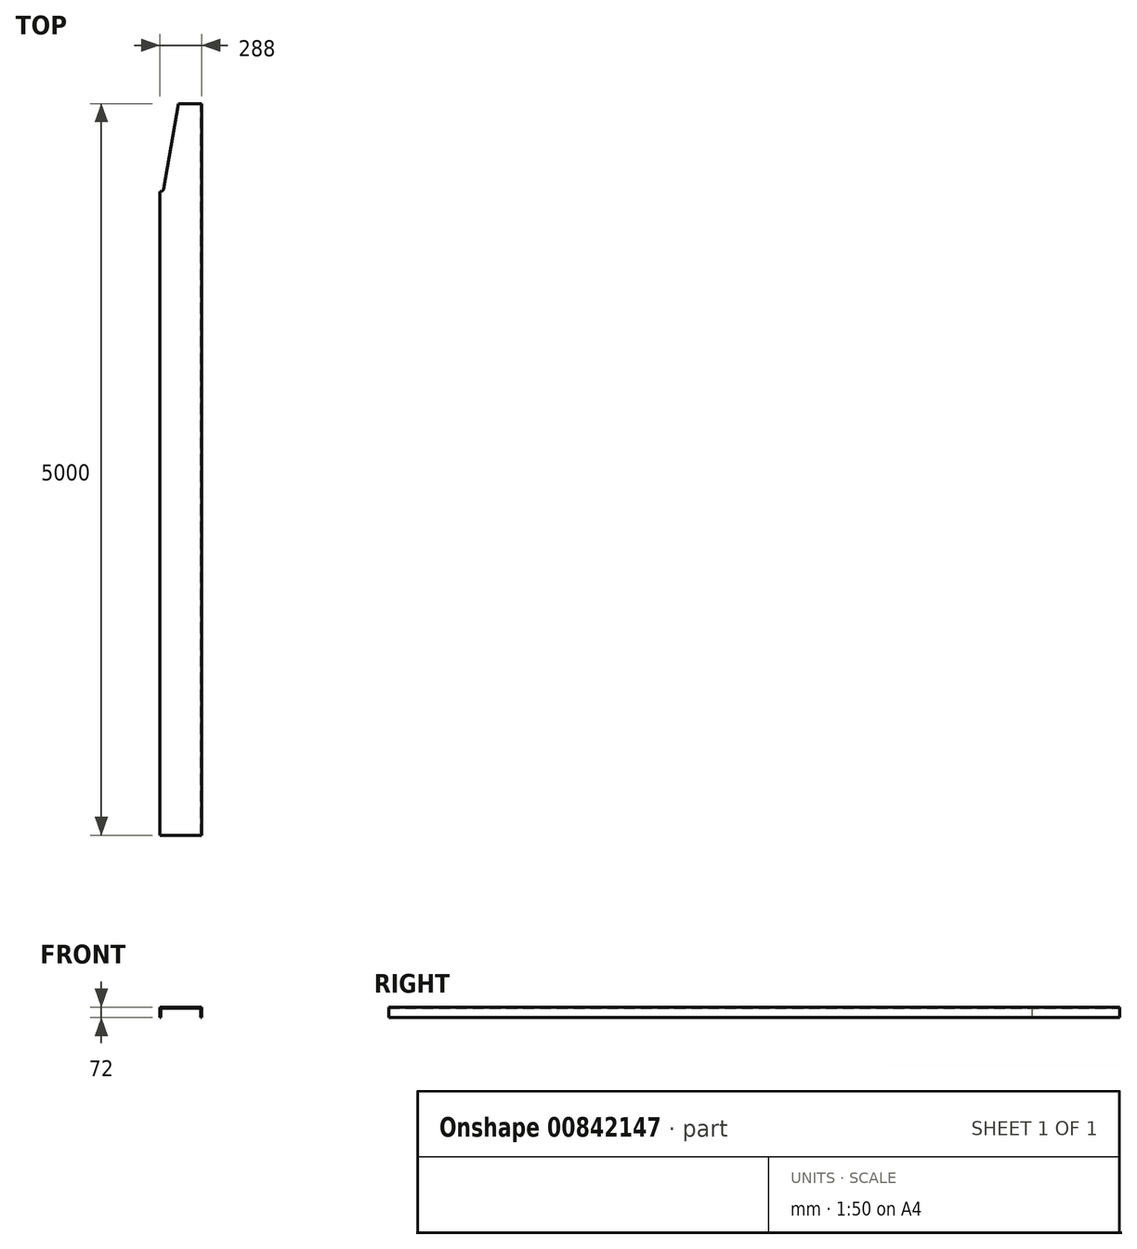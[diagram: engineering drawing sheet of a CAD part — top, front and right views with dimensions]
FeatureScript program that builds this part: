
annotation { "Feature Type Name" : "Feature", "Feature Type Description" : "" }
export const myFeature = defineFeature(function(context is Context, id is Id, definition is map)
    precondition{}
    {
        {
            var Q0;
            Q0=qCreatedBy(makeId("Front.planeOp"),FACE);
            var sketch = newSketch(context, id + "F0", { "sketchPlane" : qUnion([Q0])});
            skLineSegment(sketch, "E0", {"start": v(0, 8) * mm, "end": v(-144, 8) * mm});
            skLineSegment(sketch, "E1", {"start": v(-144, 8) * mm, "end": v(-144, -64) * mm});
            skLineSegment(sketch, "E2", {"start": v(-144, -64) * mm, "end": v(-136, -64) * mm});
            skLineSegment(sketch, "E3", {"start": v(-136, -64) * mm, "end": v(-136, -8) * mm});
            skLineSegment(sketch, "E4", {"start": v(-128, 0) * mm, "end": v(0, 0) * mm});
            skLineSegment(sketch, "E5", {"start": v(0, 50.67) * mm, "end": v(0, -39.29) * mm, "construction": true});
            skPoint(sketch, "E6.visualSharp", {"position": v(-136, 0) * mm});
            skArc(sketch, "E6.filletArc", {"start": v(-128, 0) * mm, "mid": v(-133.66, -2.34) * mm, "end": v(-136, -8) * mm});
            skLineSegment(sketch, "E7.MirrorCS", {"start": v(144, -64) * mm, "end": v(136, -64) * mm});
            skArc(sketch, "E8.MirrorCS", {"start": v(128, 0) * mm, "mid": v(133.66, -2.34) * mm, "end": v(136, -8) * mm});
            skLineSegment(sketch, "E9.MirrorCS", {"start": v(128, 0) * mm, "end": v(0, 0) * mm});
            skLineSegment(sketch, "E10.MirrorCS", {"start": v(0, 8) * mm, "end": v(144, 8) * mm});
            skLineSegment(sketch, "E11.MirrorCS", {"start": v(136, -64) * mm, "end": v(136, -8) * mm});
            skLineSegment(sketch, "E12.MirrorCS", {"start": v(144, 8) * mm, "end": v(144, -64) * mm});
            skPoint(sketch, "E13.MirrorP", {"position": v(136, 0) * mm});
            skSolve(sketch);
        }
        {
            var Q0;
            Q0 = qSketchRegion(id + "F0", true);
            extrude(context, id + "F1", {"entities" : qUnion([Q0]), "depth" : 5000 * mm, "offsetDistance" : 25 * mm});
        }
        {
            var Q0;
            Q0=makeQuery(id+"F1.opExtrude","SWEPT_FACE",FACE,{"disambiguationData":[OSD([sQuery(id+"F0.wireOp",EDGE,"E0"),sQuery(id+"F0.wireOp",EDGE,"E10.MirrorCS")])]});
            var sketch = newSketch(context, id + "F2", { "sketchPlane" : qUnion([Q0])});
            skLineSegment(sketch, "E14", {"start": v(-16, 0) * mm, "end": v(-118.1, -583.45) * mm});
            skLineSegment(sketch, "E15", {"start": v(-137.8, -600) * mm, "end": v(-144, -600) * mm});
            skLineSegment(sketch, "E16", {"start": v(-144, -600) * mm, "end": v(-144, 0) * mm});
            skLineSegment(sketch, "E17", {"start": v(-144, 0) * mm, "end": v(-16, 0) * mm});
            skPoint(sketch, "E18.visualSharp", {"position": v(-121, -600) * mm});
            skArc(sketch, "E18.filletArc", {"start": v(-137.8, -600) * mm, "mid": v(-124.94, -595.31) * mm, "end": v(-118.1, -583.45) * mm});
            skSolve(sketch);
        }
        {
            var Q0;
            Q0 = qSketchRegion(id + "F2", true);
            extrude(context, id + "F3", {"entities" : qUnion([Q0]), "operationType" : NewBodyOperationType.REMOVE, "endBound" : BoundingType.THROUGH_ALL, "oppositeDirection" : true, "depth" : 25 * mm, "offsetDistance" : 25 * mm});
        }
    });
